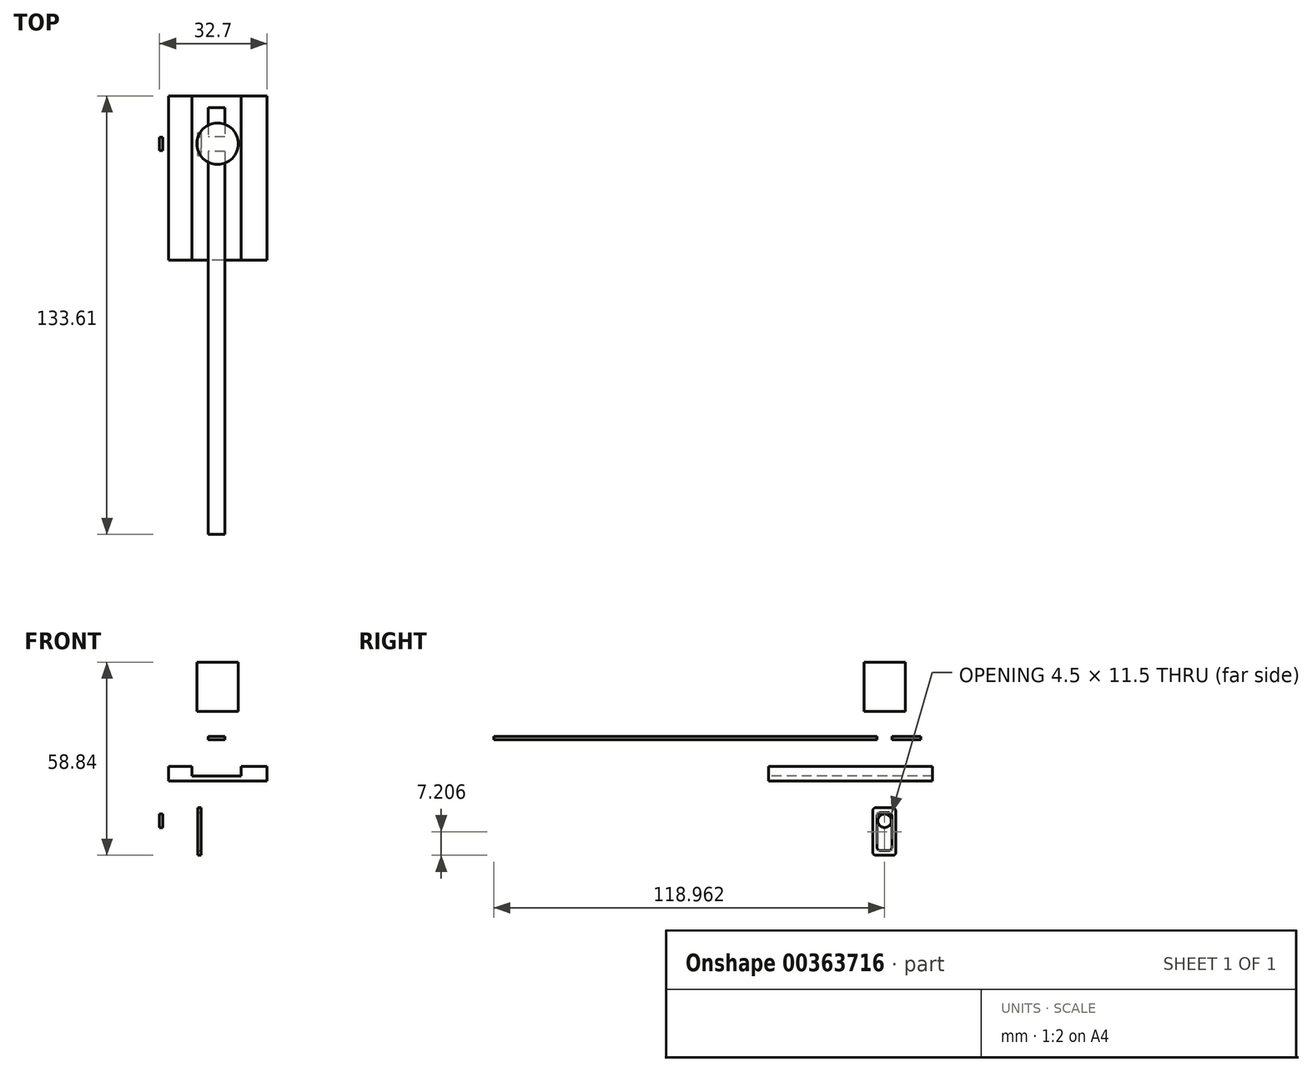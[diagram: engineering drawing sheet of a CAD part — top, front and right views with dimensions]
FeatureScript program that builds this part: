
annotation { "Feature Type Name" : "Feature", "Feature Type Description" : "" }
export const myFeature = defineFeature(function(context is Context, id is Id, definition is map)
    precondition{}
    {
        {
            var Q0;
            Q0=qCreatedBy(makeId("Right.planeOp"),FACE);
            var sketch = newSketch(context, id + "F0", { "sketchPlane" : qUnion([Q0])});
            skLineSegment(sketch, "E0.bottom", {"start": v(47.15, -12.69) * mm, "end": v(-82.85, -12.69) * mm});
            skLineSegment(sketch, "E0.top", {"start": v(47.15, -7.69) * mm, "end": v(-82.85, -7.69) * mm});
            skLineSegment(sketch, "E0.left", {"start": v(47.15, -12.69) * mm, "end": v(47.15, -7.69) * mm});
            skLineSegment(sketch, "E0.right", {"start": v(-82.85, -12.69) * mm, "end": v(-82.85, -7.69) * mm});
            skSolve(sketch);
        }
        {
            var Q0;
            Q0 = qSketchRegion(id + "F0", true);
            extrude(context, id + "F1", {"entities" : qUnion([Q0]), "depth" : 1 * mm});
        }
        {
            var Q0;
            Q0=makeQuery(id+"F1.opExtrude","SWEPT_BODY",BODY,{"disambiguationData":[OSD([sQuery(id+"F0.wireOp",EDGE,"E0.bottom"),sQuery(id+"F0.wireOp",EDGE,"E0.top"),sQuery(id+"F0.wireOp",EDGE,"E0.left"),sQuery(id+"F0.wireOp",EDGE,"E0.right")])]});
            transform(context, id + "F2", {"entities" : qUnion([Q0]), "transformType" : TransformType.TRANSLATION_3D, "dx" : -16.6 * mm, "dy" : 0 * mm, "dz" : 0 * mm, "makeCopy" : false});
        }
        {
            var Q0;
            Q0=qCreatedBy(makeId("Right.planeOp"),FACE);
            var sketch = newSketch(context, id + "F3", { "sketchPlane" : qUnion([Q0])});
            skLineSegment(sketch, "E1.bottom", {"start": v(50.76, 5.17) * mm, "end": v(0.76, 5.17) * mm});
            skLineSegment(sketch, "E1.top", {"start": v(50.76, -24.83) * mm, "end": v(0.76, -24.83) * mm});
            skLineSegment(sketch, "E1.left", {"start": v(50.76, 5.17) * mm, "end": v(50.76, -24.83) * mm});
            skLineSegment(sketch, "E1.right", {"start": v(0.76, 5.17) * mm, "end": v(0.76, -24.83) * mm});
            skSolve(sketch);
        }
        {
            var Q0;
            Q0 = qSketchRegion(id + "F3", true);
            extrude(context, id + "F4", {"entities" : qUnion([Q0]), "depth" : 4.5 * mm});
        }
        {
            var Q0;
            Q0=qCreatedBy(makeId("Right.planeOp"),FACE);
            var sketch = newSketch(context, id + "F5", { "sketchPlane" : qUnion([Q0])});
            skLineSegment(sketch, "E2.bottom", {"start": v(63.05, -27.89) * mm, "end": v(3.05, -27.89) * mm});
            skLineSegment(sketch, "E2.top", {"start": v(63.05, -42.89) * mm, "end": v(3.05, -42.89) * mm});
            skLineSegment(sketch, "E2.left", {"start": v(63.05, -27.89) * mm, "end": v(63.05, -42.89) * mm});
            skLineSegment(sketch, "E2.right", {"start": v(3.05, -27.89) * mm, "end": v(3.05, -42.89) * mm});
            skSolve(sketch);
        }
        {
            var Q0;
            Q0=makeQuery(id+"F5.imprint","IMPRINT",FACE,{"disambiguationData":[TD([[makeQuery(id+"F5.imprint","IMPRINT",EDGE,{"derivedFrom":sQuery(id+"F5.wireOp",EDGE,"E2.bottom")}),1.0]])]});
            extrude(context, id + "F6", {"entities" : qUnion([Q0]), "depth" : 2.6 * mm});
        }
        {
            var Q0;
            Q0=makeQuery(id+"F6.opExtrude","SWEPT_BODY",BODY,{"disambiguationData":[OSD([sQuery(id+"F5.wireOp",EDGE,"E2.bottom"),sQuery(id+"F5.wireOp",EDGE,"E2.top"),sQuery(id+"F5.wireOp",EDGE,"E2.left"),sQuery(id+"F5.wireOp",EDGE,"E2.right")])]});
            transform(context, id + "F7", {"entities" : qUnion([Q0]), "transformType" : TransformType.TRANSLATION_3D, "dx" : 0 * mm, "dy" : -6.9 * mm, "dz" : 25.2 * mm, "makeCopy" : false});
        }
        {
            var Q0;
            Q0=makeQuery(id+"F6.opExtrude","CAP_FACE",FACE,{"disambiguationData":[OSD([sQuery(id+"F5.wireOp",EDGE,"E2.bottom"),sQuery(id+"F5.wireOp",EDGE,"E2.top"),sQuery(id+"F5.wireOp",EDGE,"E2.left"),sQuery(id+"F5.wireOp",EDGE,"E2.right")])],"isStart":true});
            extrude(context, id + "F8", {"entities" : qUnion([Q0]), "operationType" : NewBodyOperationType.REMOVE, "oppositeDirection" : true, "depth" : 2.9 * mm});
        }
        {
            var Q0;
            Q0=qCreatedBy(makeId("Right.planeOp"),FACE);
            var sketch = newSketch(context, id + "F9", { "sketchPlane" : qUnion([Q0])});
            skLineSegment(sketch, "E3.bottom", {"start": v(39.54, -3.82) * mm, "end": v(32.54, -3.82) * mm});
            skLineSegment(sketch, "E3.top", {"start": v(39.54, -18.37) * mm, "end": v(32.54, -18.37) * mm});
            skLineSegment(sketch, "E3.left", {"start": v(39.54, -3.82) * mm, "end": v(39.54, -18.37) * mm});
            skLineSegment(sketch, "E3.right", {"start": v(32.54, -3.82) * mm, "end": v(32.54, -18.37) * mm});
            skSolve(sketch);
        }
        {
            var Q0;
            Q0 = qSketchRegion(id + "F9", true);
            extrude(context, id + "F10", {"entities" : qUnion([Q0]), "oppositeDirection" : true, "depth" : 1 * mm});
        }
        {
            var Q0;
            Q0=makeQuery(id+"F10.opExtrude","SWEPT_BODY",BODY,{"disambiguationData":[OSD([sQuery(id+"F9.wireOp",EDGE,"E3.bottom"),sQuery(id+"F9.wireOp",EDGE,"E3.top"),sQuery(id+"F9.wireOp",EDGE,"E3.left"),sQuery(id+"F9.wireOp",EDGE,"E3.right")])]});
            transform(context, id + "F11", {"entities" : qUnion([Q0]), "transformType" : TransformType.TRANSLATION_3D, "dx" : -44.1 * mm, "dy" : 0 * mm, "dz" : 0 * mm, "makeCopy" : false});
        }
        {
            var Q0;
            Q0=makeQuery(id+"F10.opExtrude","SWEPT_BODY",BODY,{"disambiguationData":[OSD([sQuery(id+"F9.wireOp",EDGE,"E3.bottom"),sQuery(id+"F9.wireOp",EDGE,"E3.top"),sQuery(id+"F9.wireOp",EDGE,"E3.left"),sQuery(id+"F9.wireOp",EDGE,"E3.right")])]});
            transform(context, id + "F12", {"entities" : qUnion([Q0]), "transformType" : TransformType.TRANSLATION_3D, "dx" : 0 * mm, "dy" : 0 * mm, "dz" : 0.9 * mm, "makeCopy" : false});
        }
        {
            var Q0;
            Q0=makeQuery(id+"F10.opExtrude","SWEPT_EDGE",EDGE,{"disambiguationData":[OSD([sQuery(id+"F9.wireOp",EDGE,"E3.bottom"),sQuery(id+"F9.wireOp",EDGE,"E3.left")])]});
            fillet(context, id + "F13", {"entities" : qUnion([Q0]), "radius" : 1 * mm, "tangentPropagation" : true, "allowEdgeOverflow" : false});
        }
        {
            var Q0;
            Q0=makeQuery(id+"F10.opExtrude","SWEPT_EDGE",EDGE,{"disambiguationData":[OSD([sQuery(id+"F9.wireOp",EDGE,"E3.bottom"),sQuery(id+"F9.wireOp",EDGE,"E3.right")])]});
            fillet(context, id + "F14", {"entities" : qUnion([Q0]), "radius" : 1 * mm, "tangentPropagation" : true, "allowEdgeOverflow" : false});
        }
        {
            var Q0;
            Q0=makeQuery(id+"F10.opExtrude","SWEPT_EDGE",EDGE,{"disambiguationData":[OSD([sQuery(id+"F9.wireOp",EDGE,"E3.top"),sQuery(id+"F9.wireOp",EDGE,"E3.left")])]});
            fillet(context, id + "F15", {"entities" : qUnion([Q0]), "radius" : 0.8 * mm, "tangentPropagation" : true, "allowEdgeOverflow" : false});
        }
        {
            var Q0;
            Q0=makeQuery(id+"F10.opExtrude","SWEPT_EDGE",EDGE,{"disambiguationData":[OSD([sQuery(id+"F9.wireOp",EDGE,"E3.top"),sQuery(id+"F9.wireOp",EDGE,"E3.right")])]});
            fillet(context, id + "F16", {"entities" : qUnion([Q0]), "radius" : 1 * mm, "tangentPropagation" : true, "allowEdgeOverflow" : false});
        }
        {
            var Q0;
            Q0=qCreatedBy(makeId("Right.planeOp"),FACE);
            var sketch = newSketch(context, id + "F17", { "sketchPlane" : qUnion([Q0])});
            skLineSegment(sketch, "E4.bottom", {"start": v(38.26, -4.61) * mm, "end": v(33.76, -4.61) * mm});
            skLineSegment(sketch, "E4.top", {"start": v(38.26, -16.11) * mm, "end": v(33.76, -16.11) * mm});
            skLineSegment(sketch, "E4.left", {"start": v(38.26, -4.61) * mm, "end": v(38.26, -16.11) * mm});
            skLineSegment(sketch, "E4.right", {"start": v(33.76, -4.61) * mm, "end": v(33.76, -16.11) * mm});
            skSolve(sketch);
        }
        {
            var Q0;
            Q0=makeQuery(id+"F17.imprint","IMPRINT",FACE,{"disambiguationData":[TD([[makeQuery(id+"F17.imprint","IMPRINT",EDGE,{"derivedFrom":sQuery(id+"F17.wireOp",EDGE,"E4.bottom")}),1.0]])]});
            extrude(context, id + "F18", {"entities" : qUnion([Q0]), "depth" : 1 * mm});
        }
        {
            var Q0;
            Q0=makeQuery(id+"F18.opExtrude","SWEPT_BODY",BODY,{"disambiguationData":[OSD([sQuery(id+"F17.wireOp",EDGE,"E4.bottom"),sQuery(id+"F17.wireOp",EDGE,"E4.top"),sQuery(id+"F17.wireOp",EDGE,"E4.left"),sQuery(id+"F17.wireOp",EDGE,"E4.right")])]});
            transform(context, id + "F19", {"entities" : qUnion([Q0]), "transformType" : TransformType.TRANSLATION_3D, "dx" : -42.3 * mm, "dy" : 0.1 * mm, "dz" : 0.1 * mm, "makeCopy" : false});
        }
        {
            var Q0;
            Q0=makeQuery(id+"F18.opExtrude","SWEPT_EDGE",EDGE,{"disambiguationData":[OSD([sQuery(id+"F17.wireOp",EDGE,"E4.bottom"),sQuery(id+"F17.wireOp",EDGE,"E4.right")])]});
            fillet(context, id + "F20", {"entities" : qUnion([Q0]), "radius" : 1 * mm, "tangentPropagation" : true, "allowEdgeOverflow" : false});
        }
        {
            var Q0;
            Q0=makeQuery(id+"F18.opExtrude","SWEPT_EDGE",EDGE,{"disambiguationData":[OSD([sQuery(id+"F17.wireOp",EDGE,"E4.bottom"),sQuery(id+"F17.wireOp",EDGE,"E4.left")])]});
            fillet(context, id + "F21", {"entities" : qUnion([Q0]), "radius" : 1 * mm, "tangentPropagation" : true, "allowEdgeOverflow" : false});
        }
        {
            var Q0;
            Q0=makeQuery(id+"F18.opExtrude","SWEPT_EDGE",EDGE,{"disambiguationData":[OSD([sQuery(id+"F17.wireOp",EDGE,"E4.top"),sQuery(id+"F17.wireOp",EDGE,"E4.right")])]});
            fillet(context, id + "F22", {"entities" : qUnion([Q0]), "radius" : 1 * mm, "tangentPropagation" : true, "allowEdgeOverflow" : false});
        }
        {
            var Q0;
            Q0=makeQuery(id+"F18.opExtrude","SWEPT_EDGE",EDGE,{"disambiguationData":[OSD([sQuery(id+"F17.wireOp",EDGE,"E4.top"),sQuery(id+"F17.wireOp",EDGE,"E4.left")])]});
            fillet(context, id + "F23", {"entities" : qUnion([Q0]), "radius" : 1 * mm, "tangentPropagation" : true, "allowEdgeOverflow" : false});
        }
        {
            var Q0;
            Q0=makeQuery(id+"F18.opExtrude","CAP_FACE",FACE,{"disambiguationData":[OSD([sQuery(id+"F17.wireOp",EDGE,"E4.bottom"),sQuery(id+"F17.wireOp",EDGE,"E4.top"),sQuery(id+"F17.wireOp",EDGE,"E4.left"),sQuery(id+"F17.wireOp",EDGE,"E4.right")])],"isStart":true});
            extrude(context, id + "F24", {"entities" : qUnion([Q0]), "operationType" : NewBodyOperationType.REMOVE, "endBound" : BoundingType.THROUGH_ALL, "depth" : 7.3 * mm});
        }
        {
            var Q0;
            Q0=makeQuery(id+"F10.opExtrude","SWEPT_BODY",BODY,{"disambiguationData":[OSD([sQuery(id+"F9.wireOp",EDGE,"E3.bottom"),sQuery(id+"F9.wireOp",EDGE,"E3.top"),sQuery(id+"F9.wireOp",EDGE,"E3.left"),sQuery(id+"F9.wireOp",EDGE,"E3.right")])]});
            transform(context, id + "F25", {"entities" : qUnion([Q0]), "transformType" : TransformType.TRANSLATION_3D, "dx" : 28.5 * mm, "dy" : 0 * mm, "dz" : 0 * mm, "makeCopy" : false});
        }
        {
            var Q0;
            Q0=makeQuery(id+"F18.opExtrude","SWEPT_BODY",BODY,{"disambiguationData":[OSD([sQuery(id+"F17.wireOp",EDGE,"E4.bottom"),sQuery(id+"F17.wireOp",EDGE,"E4.top"),sQuery(id+"F17.wireOp",EDGE,"E4.left"),sQuery(id+"F17.wireOp",EDGE,"E4.right")])]});
            transform(context, id + "F26", {"entities" : qUnion([Q0]), "transformType" : TransformType.TRANSLATION_3D, "dx" : 25.7 * mm, "dy" : 0 * mm, "dz" : -0.08 * mm, "makeCopy" : false});
        }
        {
            var Q0;
            Q0=makeQuery(id+"F18.opExtrude","SWEPT_BODY",BODY,{"disambiguationData":[OSD([sQuery(id+"F17.wireOp",EDGE,"E4.bottom"),sQuery(id+"F17.wireOp",EDGE,"E4.top"),sQuery(id+"F17.wireOp",EDGE,"E4.left"),sQuery(id+"F17.wireOp",EDGE,"E4.right")])]});
            var Q1;
            Q1=makeQuery(id+"F1.opExtrude","SWEPT_BODY",BODY,{"disambiguationData":[OSD([sQuery(id+"F0.wireOp",EDGE,"E0.bottom"),sQuery(id+"F0.wireOp",EDGE,"E0.top"),sQuery(id+"F0.wireOp",EDGE,"E0.left"),sQuery(id+"F0.wireOp",EDGE,"E0.right")])]});
            booleanBodies(context, id + "F27", {"operationType" : BooleanOperationType.SUBTRACTION, "tools" : qUnion([Q0]), "targets" : qUnion([Q1])});
        }
        {
            var Q0;
            Q0=qCreatedBy(makeId("Right.planeOp"),FACE);
            var sketch = newSketch(context, id + "F28", { "sketchPlane" : qUnion([Q0])});
            skCircle(sketch, "E5", {"center": v(39.02, -9.87) * mm, "radius": 6.33 * mm});
            skPoint(sketch, "E5.first.point", {"position": v(44.15, -6.16) * mm});
            skPoint(sketch, "E5.second.point", {"position": v(35.8, -15.31) * mm});
            skPoint(sketch, "E5.third.point", {"position": v(33.4, -6.96) * mm});
            skSolve(sketch);
        }
        {
            var Q0;
            Q0=makeQuery(id+"F28.imprint","IMPRINT",FACE,{"disambiguationData":[TD([[makeQuery(id+"F28.imprint","IMPRINT",EDGE,{"derivedFrom":sQuery(id+"F28.wireOp",EDGE,"E5")}),1.0]])]});
            extrude(context, id + "F29", {"entities" : qUnion([Q0]), "oppositeDirection" : true, "depth" : 15 * mm});
        }
        {
            var Q0;
            Q0=makeQuery(id+"F29.opExtrude","SWEPT_BODY",BODY,{"disambiguationData":[OSD([sQuery(id+"F28.wireOp",EDGE,"E5")])]});
            transform(context, id + "F30", {"entities" : qUnion([Q0]), "transformType" : TransformType.TRANSLATION_3D, "dx" : -28.1 * mm, "dy" : -2.8 * mm, "dz" : 0 * mm, "makeCopy" : false});
        }
        {
            var Q0;
            Q0=qCreatedBy(makeId("Right.planeOp"),FACE);
            var sketch = newSketch(context, id + "F31", { "sketchPlane" : qUnion([Q0])});
            skCircle(sketch, "E6", {"center": v(36.15, -6.95) * mm, "radius": 2.06 * mm});
            skPoint(sketch, "E6.first.point", {"position": v(36.12, -4.9) * mm});
            skPoint(sketch, "E6.second.point", {"position": v(36.12, -9) * mm});
            skPoint(sketch, "E6.third.point", {"position": v(37.35, -8.61) * mm});
            skSolve(sketch);
        }
        {
            var Q0;
            Q0=makeQuery(id+"F31.imprint","IMPRINT",FACE,{"disambiguationData":[TD([[makeQuery(id+"F31.imprint","IMPRINT",EDGE,{"derivedFrom":sQuery(id+"F31.wireOp",EDGE,"E6")}),1.0]])]});
            extrude(context, id + "F32", {"entities" : qUnion([Q0]), "depth" : 1 * mm});
        }
        {
            var Q0;
            Q0=makeQuery(id+"F32.opExtrude","SWEPT_BODY",BODY,{"disambiguationData":[OSD([sQuery(id+"F31.wireOp",EDGE,"E6")])]});
            transform(context, id + "F33", {"entities" : qUnion([Q0]), "transformType" : TransformType.TRANSLATION_3D, "dx" : -28.2 * mm, "dy" : 0 * mm, "dz" : 0 * mm, "makeCopy" : false});
        }
        {
            var Q0;
            Q0=makeQuery(id+"F29.opExtrude","SWEPT_BODY",BODY,{"disambiguationData":[OSD([sQuery(id+"F28.wireOp",EDGE,"E5")])]});
            transform(context, id + "F34", {"entities" : qUnion([Q0]), "transformType" : TransformType.TRANSLATION_3D, "dx" : 11.4 * mm, "dy" : 0 * mm, "dz" : 0 * mm, "makeCopy" : false});
        }
        {
            var Q0;
            Q0=makeQuery(id+"F1.opExtrude","SWEPT_BODY",BODY,{"disambiguationData":[OSD([sQuery(id+"F0.wireOp",EDGE,"E0.bottom"),sQuery(id+"F0.wireOp",EDGE,"E0.top"),sQuery(id+"F0.wireOp",EDGE,"E0.left"),sQuery(id+"F0.wireOp",EDGE,"E0.right")])]});
            transform(context, id + "F35", {"entities" : qUnion([Q0]), "transformType" : TransformType.TRANSLATION_3D, "dx" : 7.5 * mm, "dy" : 0 * mm, "dz" : 0 * mm, "makeCopy" : false});
        }
        {
            var Q0;
            Q0=makeQuery(id+"F1.opExtrude","SWEPT_BODY",BODY,{"disambiguationData":[OSD([sQuery(id+"F0.wireOp",EDGE,"E0.bottom"),sQuery(id+"F0.wireOp",EDGE,"E0.top"),sQuery(id+"F0.wireOp",EDGE,"E0.left"),sQuery(id+"F0.wireOp",EDGE,"E0.right")])]});
            var Q1;
            Q1=makeQuery(id+"F4.opExtrude","SWEPT_BODY",BODY,{"disambiguationData":[OSD([sQuery(id+"F3.wireOp",EDGE,"E1.bottom"),sQuery(id+"F3.wireOp",EDGE,"E1.top"),sQuery(id+"F3.wireOp",EDGE,"E1.left"),sQuery(id+"F3.wireOp",EDGE,"E1.right")])]});
            var Q2;
            Q2=makeQuery(id+"F29.opExtrude","SWEPT_BODY",BODY,{"disambiguationData":[OSD([sQuery(id+"F28.wireOp",EDGE,"E5")])]});
            var Q3;
            Q3=makeQuery(id+"F4.opExtrude","CAP_EDGE",EDGE,{"disambiguationData":[OSD([sQuery(id+"F3.wireOp",EDGE,"E1.bottom")])],"isStart":false});
            transform(context, id + "F36", {"entities" : qUnion([Q0, Q1, Q2]), "transformType" : TransformType.ROTATION, "transformAxis" : qUnion([Q3]), "angle" : 90 * degree, "oppositeDirection" : true, "makeCopy" : false});
        }
    });
